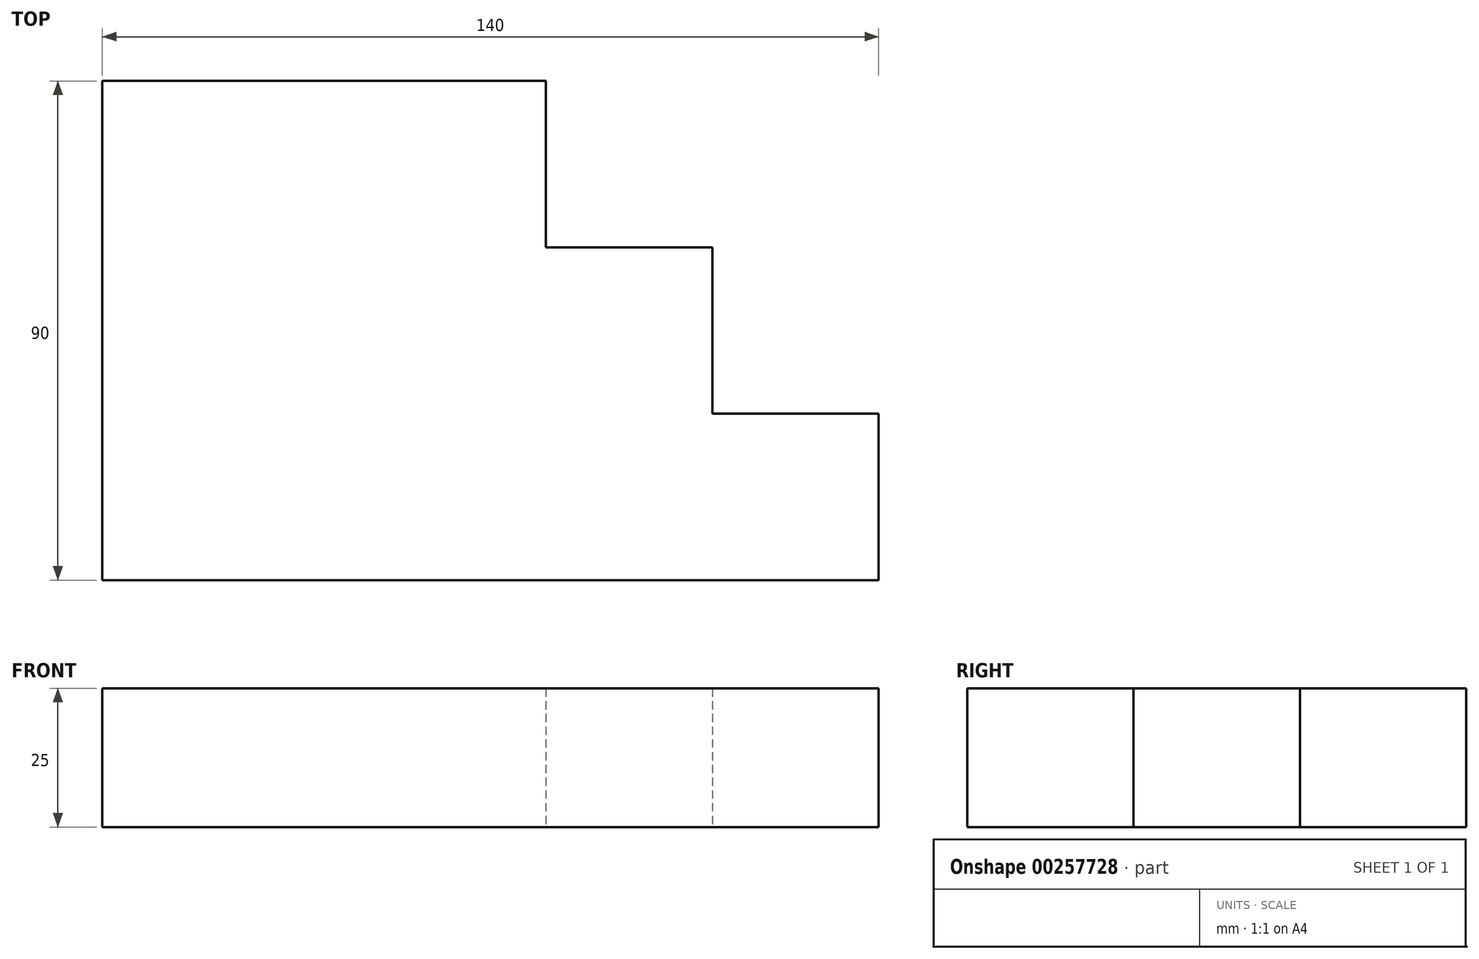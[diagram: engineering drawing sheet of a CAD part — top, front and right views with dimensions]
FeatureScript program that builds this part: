
annotation { "Feature Type Name" : "Feature", "Feature Type Description" : "" }
export const myFeature = defineFeature(function(context is Context, id is Id, definition is map)
    precondition{}
    {
        {
            var Q0;
            Q0=qCreatedBy(makeId("Top.planeOp"),FACE);
            var sketch = newSketch(context, id + "F0", { "sketchPlane" : qUnion([Q0])});
            skLineSegment(sketch, "E0", {"start": v(-40.1, -30.23) * mm, "end": v(99.9, -30.23) * mm});
            skLineSegment(sketch, "E1", {"start": v(-40.1, -30.23) * mm, "end": v(-40.1, 59.77) * mm});
            skLineSegment(sketch, "E2", {"start": v(-40.1, 59.77) * mm, "end": v(39.9, 59.77) * mm});
            skLineSegment(sketch, "E3", {"start": v(39.9, 59.77) * mm, "end": v(39.9, 29.77) * mm});
            skLineSegment(sketch, "E4", {"start": v(39.9, 29.77) * mm, "end": v(69.9, 29.77) * mm});
            skLineSegment(sketch, "E5", {"start": v(69.9, 29.77) * mm, "end": v(69.9, -0.23) * mm});
            skLineSegment(sketch, "E6", {"start": v(69.9, -0.23) * mm, "end": v(99.9, -0.23) * mm});
            skLineSegment(sketch, "E7", {"start": v(99.9, -0.23) * mm, "end": v(99.9, -30.23) * mm});
            skLineSegment(sketch, "E8", {"start": v(-40.1, -60.67) * mm, "end": v(-40.1, -110.67) * mm});
            skLineSegment(sketch, "E9", {"start": v(-20.1, -130.67) * mm, "end": v(89.9, -130.67) * mm});
            skLineSegment(sketch, "E10", {"start": v(99.9, -120.67) * mm, "end": v(99.9, -110.67) * mm});
            skLineSegment(sketch, "E11", {"start": v(89.9, -100.67) * mm, "end": v(79.9, -100.67) * mm});
            skLineSegment(sketch, "E12", {"start": v(69.9, -90.67) * mm, "end": v(69.9, -80.67) * mm});
            skLineSegment(sketch, "E13", {"start": v(59.9, -70.67) * mm, "end": v(49.9, -70.67) * mm});
            skLineSegment(sketch, "E14", {"start": v(39.9, -60.67) * mm, "end": v(39.9, -50.67) * mm});
            skLineSegment(sketch, "E15", {"start": v(29.9, -40.67) * mm, "end": v(-20.1, -40.67) * mm});
            skPoint(sketch, "E16.visualSharp", {"position": v(-40.1, -40.67) * mm});
            skArc(sketch, "E16.filletArc", {"start": v(-20.1, -40.67) * mm, "mid": v(-34.25, -46.53) * mm, "end": v(-40.1, -60.67) * mm});
            skPoint(sketch, "E17.visualSharp", {"position": v(99.9, -130.67) * mm});
            skArc(sketch, "E17.filletArc", {"start": v(89.9, -130.67) * mm, "mid": v(96.96, -127.74) * mm, "end": v(99.9, -120.67) * mm});
            skPoint(sketch, "E18.visualSharp", {"position": v(99.9, -100.67) * mm});
            skArc(sketch, "E18.filletArc", {"start": v(99.9, -110.67) * mm, "mid": v(96.96, -103.6) * mm, "end": v(89.9, -100.67) * mm});
            skPoint(sketch, "E19.visualSharp", {"position": v(69.9, -70.67) * mm});
            skArc(sketch, "E19.filletArc", {"start": v(69.9, -80.67) * mm, "mid": v(66.96, -73.6) * mm, "end": v(59.9, -70.67) * mm});
            skPoint(sketch, "E20.visualSharp", {"position": v(39.9, -40.67) * mm});
            skArc(sketch, "E20.filletArc", {"start": v(39.9, -50.67) * mm, "mid": v(36.96, -43.6) * mm, "end": v(29.9, -40.67) * mm});
            skPoint(sketch, "E21.visualSharp", {"position": v(39.9, -70.67) * mm});
            skArc(sketch, "E21.filletArc", {"start": v(39.9, -60.67) * mm, "mid": v(42.82, -67.74) * mm, "end": v(49.9, -70.67) * mm});
            skPoint(sketch, "E22.visualSharp", {"position": v(69.9, -100.67) * mm});
            skArc(sketch, "E22.filletArc", {"start": v(69.9, -90.67) * mm, "mid": v(72.82, -97.74) * mm, "end": v(79.9, -100.67) * mm});
            skPoint(sketch, "E23.visualSharp", {"position": v(-40.1, -130.67) * mm});
            skArc(sketch, "E23.filletArc", {"start": v(-40.1, -110.67) * mm, "mid": v(-34.25, -124.82) * mm, "end": v(-20.1, -130.67) * mm});
            skCircle(sketch, "E24", {"center": v(-20.1, -110.67) * mm, "radius": 10 * mm});
            skCircle(sketch, "E25", {"center": v(-20.1, -60.67) * mm, "radius": 10 * mm});
            skCircle(sketch, "E26", {"center": v(29.9, -50.67) * mm, "radius": 5 * mm});
            skCircle(sketch, "E27", {"center": v(59.9, -80.67) * mm, "radius": 5 * mm});
            skCircle(sketch, "E28", {"center": v(89.9, -110.67) * mm, "radius": 5 * mm});
            skSolve(sketch);
        }
        {
            var Q0;
            Q0=makeQuery(id+"F0.imprint","IMPRINT",FACE,{"disambiguationData":[TD([[makeQuery(id+"F0.imprint","IMPRINT",EDGE,{"derivedFrom":sQuery(id+"F0.wireOp",EDGE,"E0")}),1.0]])]});
            extrude(context, id + "F1", {"entities" : qUnion([Q0]), "depth" : 25 * mm});
        }
    });
